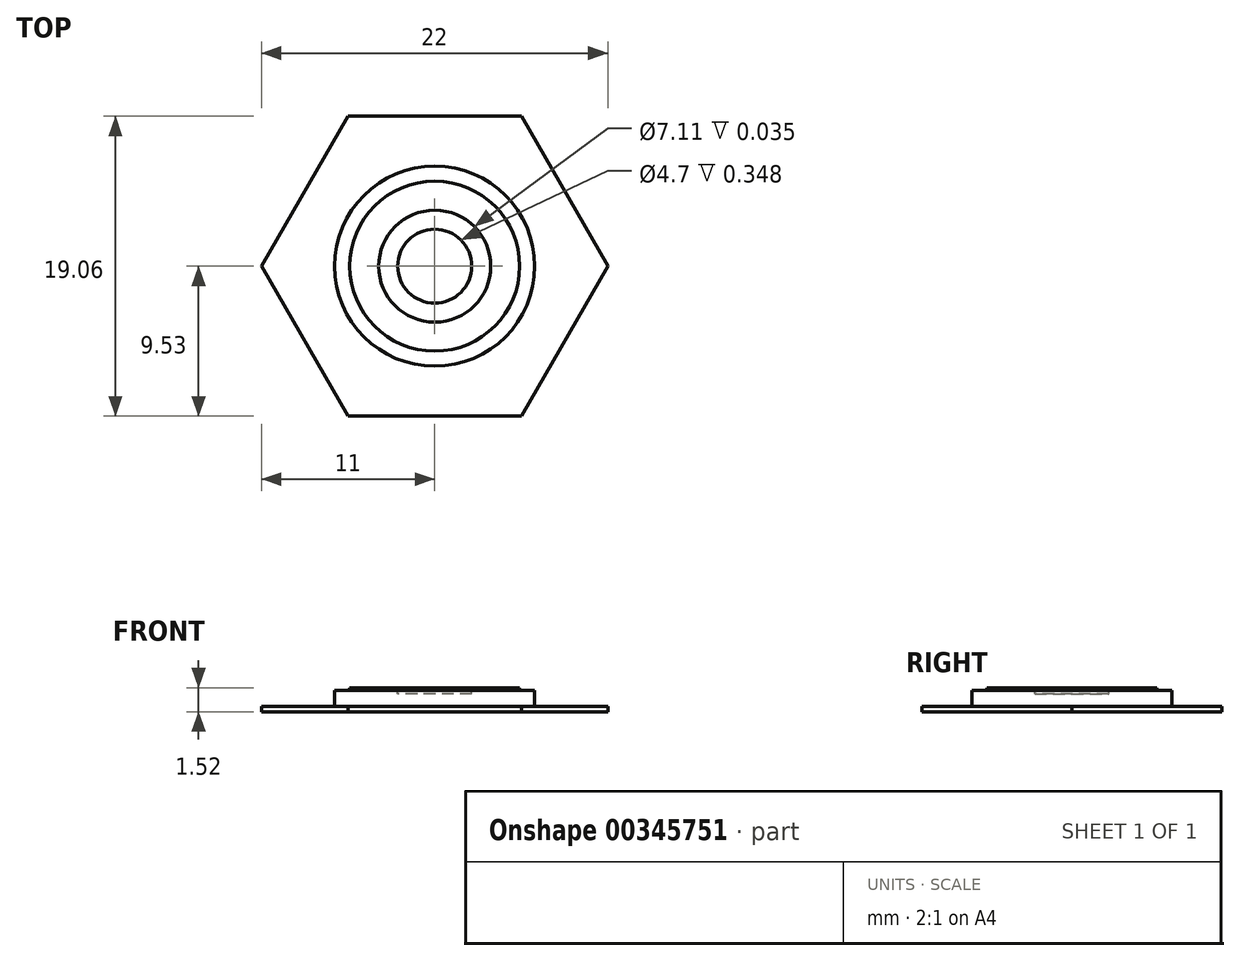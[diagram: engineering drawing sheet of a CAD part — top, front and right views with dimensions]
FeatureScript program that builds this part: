
annotation { "Feature Type Name" : "Feature", "Feature Type Description" : "" }
export const myFeature = defineFeature(function(context is Context, id is Id, definition is map)
    precondition{}
    {
        {
            assignVariable(context, id + "F0", {"name" : "HexThick", "anyValue" : 0.35});
        }
        {
            assignVariable(context, id + "F1", {"name" : "ThreadLength", "anyValue" : 1});
        }
        {
            assignVariable(context, id + "F2", {"name" : "ShaftLength", "anyValue" : 0.17});
        }
        {
            assignVariable(context, id + "F3", {"name" : "IndentDepth", "anyValue" : 0.04});
        }
        {
            assignVariable(context, id + "F4", {"name" : "HoleDepth", "anyValue" : 0.38});
        }
        {
            var Q0;
            Q0=qCreatedBy(makeId("Top.planeOp"),FACE);
            var sketch = newSketch(context, id + "F5", { "sketchPlane" : qUnion([Q0])});
            skCircle(sketch, "E0.cCircle", {"center": v(0, 0) * mm, "radius": 9.53 * mm, "construction": true});
            skLineSegment(sketch, "E0.0", {"start": v(-5.5, 9.53) * mm, "end": v(5.5, 9.53) * mm});
            skLineSegment(sketch, "E0.1", {"start": v(5.5, 9.53) * mm, "end": v(11, 0) * mm});
            skLineSegment(sketch, "E0.2", {"start": v(11, 0) * mm, "end": v(5.5, -9.52) * mm});
            skLineSegment(sketch, "E0.3", {"start": v(5.5, -9.53) * mm, "end": v(-5.5, -9.53) * mm});
            skLineSegment(sketch, "E0.4", {"start": v(-5.5, -9.52) * mm, "end": v(-11, 0) * mm});
            skLineSegment(sketch, "E0.5", {"start": v(-11, 0) * mm, "end": v(-5.5, 9.53) * mm});
            skPoint(sketch, "E0.0.midPoint", {"position": v(0, 9.53) * mm});
            skSolve(sketch);
        }
        {
            var Q0;
            Q0=makeQuery(id+"F5.imprint","IMPRINT",FACE,{"disambiguationData":[TD([[makeQuery(id+"F5.imprint","IMPRINT",EDGE,{"derivedFrom":sQuery(id+"F5.wireOp",EDGE,"E0.0")}),-1.0]])]});
            extrude(context, id + "F6", {"entities" : qUnion([Q0]), "depth" : (getVariable(context, 'HexThick')) * mm});
        }
        {
            var Q0;
            Q0=makeQuery(id+"F6.opExtrude","CAP_FACE",FACE,{"disambiguationData":[OSD([sQuery(id+"F5.wireOp",EDGE,"E0.0"),sQuery(id+"F5.wireOp",EDGE,"E0.1"),sQuery(id+"F5.wireOp",EDGE,"E0.2"),sQuery(id+"F5.wireOp",EDGE,"E0.3"),sQuery(id+"F5.wireOp",EDGE,"E0.4"),sQuery(id+"F5.wireOp",EDGE,"E0.5")])],"isStart":false});
            var sketch = newSketch(context, id + "F7", { "sketchPlane" : qUnion([Q0])});
            skCircle(sketch, "E1", {"center": v(0, 0) * mm, "radius": 6.35 * mm});
            skSolve(sketch);
        }
        {
            var Q0;
            Q0 = qSketchRegion(id + "F7", true);
            extrude(context, id + "F8", {"entities" : qUnion([Q0]), "operationType" : NewBodyOperationType.ADD, "depth" : (getVariable(context, 'ThreadLength')) * mm});
        }
        {
            var Q0;
            Q0=makeQuery(id+"F8.opExtrude","CAP_FACE",FACE,{"disambiguationData":[OSD([sQuery(id+"F7.wireOp",EDGE,"E1")])],"isStart":false});
            var sketch = newSketch(context, id + "F9", { "sketchPlane" : qUnion([Q0])});
            skCircle(sketch, "E2", {"center": v(0, 0) * mm, "radius": 5.4 * mm});
            skSolve(sketch);
        }
        {
            var Q0;
            Q0 = qSketchRegion(id + "F9", true);
            extrude(context, id + "F10", {"entities" : qUnion([Q0]), "operationType" : NewBodyOperationType.ADD, "depth" : (getVariable(context, 'ShaftLength')) * mm});
        }
        {
            var Q0;
            Q0=makeQuery(id+"F10.opExtrude","CAP_FACE",FACE,{"disambiguationData":[OSD([sQuery(id+"F9.wireOp",EDGE,"E2")])],"isStart":false});
            var sketch = newSketch(context, id + "F11", { "sketchPlane" : qUnion([Q0])});
            skCircle(sketch, "E3", {"center": v(0, 0) * mm, "radius": 3.56 * mm});
            skSolve(sketch);
        }
        {
            var Q0;
            Q0=makeQuery(id+"F11.imprint","IMPRINT",FACE,{"disambiguationData":[TD([[makeQuery(id+"F11.imprint","IMPRINT",EDGE,{"derivedFrom":sQuery(id+"F11.wireOp",EDGE,"E3")}),1.0]])]});
            extrude(context, id + "F12", {"entities" : qUnion([Q0]), "operationType" : NewBodyOperationType.REMOVE, "oppositeDirection" : true, "depth" : (getVariable(context, 'IndentDepth')) * mm});
        }
        {
            var Q0;
            Q0=makeQuery(id+"F10.opExtrude","CAP_FACE",FACE,{"disambiguationData":[OSD([sQuery(id+"F9.wireOp",EDGE,"E2")])],"isStart":false});
            var sketch = newSketch(context, id + "F13", { "sketchPlane" : qUnion([Q0])});
            skCircle(sketch, "E4", {"center": v(0, 0) * mm, "radius": 2.35 * mm});
            skSolve(sketch);
        }
        {
            var Q0;
            Q0=makeQuery(id+"F13.imprint","IMPRINT",FACE,{"disambiguationData":[TD([[makeQuery(id+"F13.imprint","IMPRINT",EDGE,{"derivedFrom":sQuery(id+"F13.wireOp",EDGE,"E4")}),1.0]])]});
            extrude(context, id + "F14", {"entities" : qUnion([Q0]), "operationType" : NewBodyOperationType.REMOVE, "oppositeDirection" : true, "depth" : (getVariable(context, 'HoleDepth')) * mm});
        }
    });
